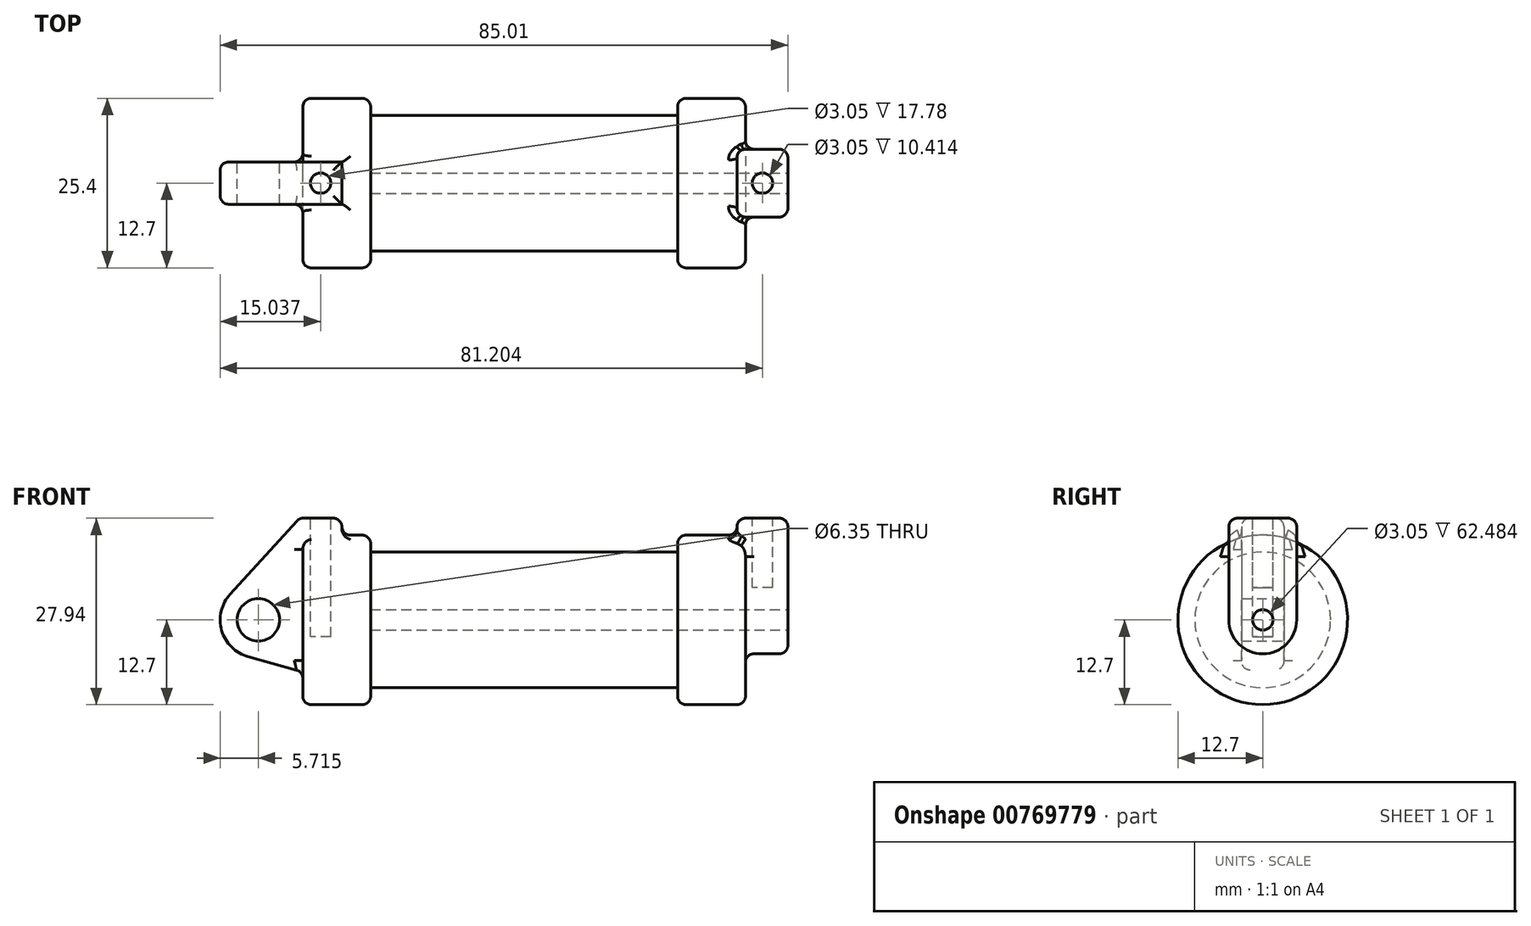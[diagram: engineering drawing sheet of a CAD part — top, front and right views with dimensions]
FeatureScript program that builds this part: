
annotation { "Feature Type Name" : "Feature", "Feature Type Description" : "" }
export const myFeature = defineFeature(function(context is Context, id is Id, definition is map)
    precondition{}
    {
        {
            var Q0;
            Q0=qCreatedBy(makeId("Front.planeOp"),FACE);
            var sketch = newSketch(context, id + "F0", { "sketchPlane" : qUnion([Q0])});
            skLineSegment(sketch, "E0", {"start": v(0, 0) * mm, "end": v(0, 12.7) * mm});
            skLineSegment(sketch, "E1", {"start": v(0, 12.7) * mm, "end": v(10.16, 12.7) * mm});
            skLineSegment(sketch, "E2", {"start": v(10.16, 12.7) * mm, "end": v(10.16, 10.16) * mm});
            skLineSegment(sketch, "E3", {"start": v(10.16, 10.16) * mm, "end": v(56.13, 10.16) * mm});
            skLineSegment(sketch, "E4", {"start": v(56.13, 10.16) * mm, "end": v(56.13, 12.7) * mm});
            skLineSegment(sketch, "E5", {"start": v(56.13, 12.7) * mm, "end": v(66.3, 12.7) * mm});
            skLineSegment(sketch, "E6", {"start": v(66.3, 12.7) * mm, "end": v(66.3, 0) * mm});
            skLineSegment(sketch, "E7", {"start": v(66.3, 0) * mm, "end": v(0, 0) * mm});
            skLineSegment(sketch, "E8", {"start": v(5.84, 15.24) * mm, "end": v(-0.5, 15.24) * mm});
            skLineSegment(sketch, "E9", {"start": v(-0.5, 15.24) * mm, "end": v(-10.88, 3.85) * mm});
            skLineSegment(sketch, "E10", {"start": v(0, 0) * mm, "end": v(-6.65, 0) * mm});
            skCircle(sketch, "E11", {"center": v(-6.65, 0) * mm, "radius": 5.72 * mm});
            skCircle(sketch, "E12", {"center": v(-6.65, 0) * mm, "radius": 3.18 * mm});
            skLineSegment(sketch, "E13", {"start": v(5.84, 15.24) * mm, "end": v(5.84, -9.4) * mm});
            skLineSegment(sketch, "E14", {"start": v(5.84, -9.4) * mm, "end": v(-8.18, -5.5) * mm});
            skSolve(sketch);
        }
        {
            var Q0;
            {var subQ0=sQuery(id+"F0.wireOp",EDGE,"E2");Q0=makeQuery(id+"F0.imprint","IMPRINT",FACE,{"disambiguationData":[TD([[makeQuery(id+"F0.imprint","IMPRINT",EDGE,{"derivedFrom":subQ0}),-1.0]])]});}
            var Q1;
            {var subQ0=sQuery(id+"F0.wireOp",EDGE,"E0");Q1=makeQuery(id+"F0.imprint","IMPRINT",FACE,{"disambiguationData":[TD([[makeQuery(id+"F0.imprint","IMPRINT",EDGE,{"derivedFrom":subQ0}),-1.0]])]});}
            var Q2;
            Q2=sQuery(id+"F0.wireOp",EDGE,"E7");
            revolve(context, id + "F1", {"surfaceOperationType" : NewSurfaceOperationType.NEW, "entities" : qUnion([Q0, Q1]), "axis" : qUnion([Q2]), "revolveType" : RevolveType.FULL});
        }
        {
            var Q0;
            {var subQ1=sQuery(id+"F0.wireOp",EDGE,"E0");Q0=makeQuery(id+"F0.imprint","IMPRINT",FACE,{"disambiguationData":[TD([[makeQuery(id+"F0.imprint","IMPRINT",EDGE,{"derivedFrom":subQ1}),1.0]])]});}
            var Q1;
            {var subQ0=sQuery(id+"F0.wireOp",EDGE,"E0");Q1=makeQuery(id+"F0.imprint","IMPRINT",FACE,{"disambiguationData":[TD([[makeQuery(id+"F0.imprint","IMPRINT",EDGE,{"derivedFrom":subQ0}),-1.0]])]});}
            var Q2;
            {var subQ0=sQuery(id+"F0.wireOp",EDGE,"E14");Q2=makeQuery(id+"F0.imprint","IMPRINT",FACE,{"disambiguationData":[TD([[makeQuery(id+"F0.imprint","IMPRINT",EDGE,{"derivedFrom":subQ0}),-1.0]])]});}
            var Q3;
            {var subQ5=sQuery(id+"F0.wireOp",EDGE,"E12");Q3=makeQuery(id+"F0.imprint","IMPRINT",FACE,{"disambiguationData":[TD([[makeQuery(id+"F0.imprint","IMPRINT",EDGE,{"derivedFrom":subQ5}),-1.0]])]});}
            extrude(context, id + "F2", {"entities" : qUnion([Q0, Q1, Q2, Q3]), "endBound" : BoundingType.SYMMETRIC, "depth" : 6.35 * mm, "offsetDistance" : 25.4 * mm});
        }
        {
            var Q0;
            Q0=makeQuery(id+"F1.opRevolve","SWEPT_BODY",BODY,{"disambiguationData":[OSD([sQuery(id+"F0.wireOp",EDGE,"E0"),sQuery(id+"F0.wireOp",EDGE,"E1"),sQuery(id+"F0.wireOp",EDGE,"E2"),sQuery(id+"F0.wireOp",EDGE,"E3"),sQuery(id+"F0.wireOp",EDGE,"E4"),sQuery(id+"F0.wireOp",EDGE,"E5"),sQuery(id+"F0.wireOp",EDGE,"E6"),sQuery(id+"F0.wireOp",EDGE,"E7")])]});
            var Q1;
            Q1=makeQuery(id+"F2.opExtrude","SWEPT_BODY",BODY,{"disambiguationData":[OSD([sQuery(id+"F0.wireOp",EDGE,"E8"),sQuery(id+"F0.wireOp",EDGE,"E9"),sQuery(id+"F0.wireOp",EDGE,"E11"),sQuery(id+"F0.wireOp",EDGE,"E12"),sQuery(id+"F0.wireOp",EDGE,"E13"),sQuery(id+"F0.wireOp",EDGE,"E14")])]});
            booleanBodies(context, id + "F3", {"operationType" : BooleanOperationType.UNION, "tools" : qUnion([Q0, Q1])});
        }
        {
            var Q0;
            Q0=makeQuery(id+"F1.opRevolve","SWEPT_FACE",FACE,{"disambiguationData":[OSD([sQuery(id+"F0.wireOp",EDGE,"E6")])]});
            var sketch = newSketch(context, id + "F4", { "sketchPlane" : qUnion([Q0])});
            skCircle(sketch, "E15", {"center": v(0, 0) * mm, "radius": 1.52 * mm});
            skCircle(sketch, "E16", {"center": v(0, 0) * mm, "radius": 5.08 * mm});
            skLineSegment(sketch, "E17", {"start": v(-5.08, 0) * mm, "end": v(-5.08, 15.24) * mm});
            skLineSegment(sketch, "E18", {"start": v(5.08, 0) * mm, "end": v(5.08, 15.24) * mm});
            skLineSegment(sketch, "E19", {"start": v(5.08, 15.24) * mm, "end": v(-5.08, 15.24) * mm});
            skSolve(sketch);
        }
        {
            var Q0;
            {var subQ0=sQuery(id+"F4.wireOp",EDGE,"E19");Q0=makeQuery(id+"F4.imprint","IMPRINT",FACE,{"disambiguationData":[TD([[makeQuery(id+"F4.imprint","IMPRINT",EDGE,{"derivedFrom":subQ0}),1.0]])]});}
            var Q1;
            {var subQ0=sQuery(id+"F4.wireOp",EDGE,"E17");var subQ1=sQuery(id+"F4.wireOp",EDGE,"E16");var subQ2=makeQuery(id+"F4.imprint","INTERSECT",VERTEX,{"derivedFrom":[subQ1,subQ0]});Q1=makeQuery(id+"F4.imprint","IMPRINT",FACE,{"disambiguationData":[TD([[makeQuery(id+"F4.imprint","IMPRINT",EDGE,{"disambiguationData":[TD([[subQ2,1.0]])],"derivedFrom":subQ1}),-1.0]])]});}
            var Q2;
            Q2=makeQuery(id+"F4.imprint","IMPRINT",FACE,{"disambiguationData":[TD([[makeQuery(id+"F4.imprint","IMPRINT",EDGE,{"derivedFrom":sQuery(id+"F4.wireOp",EDGE,"E15")}),-1.0]])]});
            extrude(context, id + "F5", {"entities" : qUnion([Q0, Q1, Q2]), "operationType" : NewBodyOperationType.ADD, "oppositeDirection" : true, "depth" : 1.27 * mm, "offsetDistance" : 25.4 * mm, "hasSecondDirection" : true, "secondDirectionOppositeDirection" : false, "secondDirectionDepth" : 6.35 * mm});
        }
        {
            var Q0;
            Q0=makeQuery(id+"F5.boolean.opBoolean","SPLIT",FACE,{"disambiguationData":[TD([makeQuery(id+"F5.opExtrude","SWEPT_FACE",FACE,{"disambiguationData":[OSD([sQuery(id+"F4.wireOp",EDGE,"E15")])]})])],"derivedFrom":makeQuery(id+"F1.opRevolve","SWEPT_FACE",FACE,{"disambiguationData":[OSD([sQuery(id+"F0.wireOp",EDGE,"E6")])]})});
            var Q1;
            Q1=makeQuery(id+"F1.opRevolve","SWEPT_FACE",FACE,{"disambiguationData":[OSD([sQuery(id+"F0.wireOp",EDGE,"E2")])]});
            extrude(context, id + "F6", {"entities" : qUnion([Q0]), "operationType" : NewBodyOperationType.REMOVE, "endBound" : BoundingType.UP_TO_SURFACE, "oppositeDirection" : true, "depth" : 25.4 * mm, "endBoundEntityFace" : qUnion([Q1]), "offsetDistance" : 25.4 * mm});
        }
        {
            var Q0;
            Q0=makeQuery(id+"F2.opExtrude","SWEPT_FACE",FACE,{"disambiguationData":[OSD([sQuery(id+"F0.wireOp",EDGE,"E8")])]});
            var sketch = newSketch(context, id + "F7", { "sketchPlane" : qUnion([Q0])});
            skCircle(sketch, "E20", {"center": v(2.67, 0) * mm, "radius": 1.52 * mm});
            skPoint(sketch, "E20.centerSnap0", {"position": v(5.84, 0) * mm});
            skPoint(sketch, "E20.centerSnap1", {"position": v(2.67, -3.18) * mm});
            skSolve(sketch);
        }
        {
            var Q0;
            Q0=makeQuery(id+"F7.imprint","IMPRINT",FACE,{"disambiguationData":[TD([[makeQuery(id+"F7.imprint","IMPRINT",EDGE,{"derivedFrom":sQuery(id+"F7.wireOp",EDGE,"E20")}),1.0]])]});
            extrude(context, id + "F8", {"entities" : qUnion([Q0]), "operationType" : NewBodyOperationType.REMOVE, "oppositeDirection" : true, "depth" : 17.78 * mm, "offsetDistance" : 25.4 * mm});
        }
        {
            var Q0;
            Q0=makeQuery(id+"F5.opExtrude","SWEPT_FACE",FACE,{"disambiguationData":[OSD([sQuery(id+"F4.wireOp",EDGE,"E19")])]});
            var sketch = newSketch(context, id + "F9", { "sketchPlane" : qUnion([Q0])});
            skCircle(sketch, "E21", {"center": v(68.83, 0) * mm, "radius": 1.52 * mm});
            skPoint(sketch, "E21.centerSnap0", {"position": v(68.83, -5.08) * mm});
            skPoint(sketch, "E21.centerSnap1", {"position": v(72.64, 0) * mm});
            skSolve(sketch);
        }
        {
            var Q0;
            Q0=makeQuery(id+"F9.imprint","IMPRINT",FACE,{"disambiguationData":[TD([[makeQuery(id+"F9.imprint","IMPRINT",EDGE,{"derivedFrom":sQuery(id+"F9.wireOp",EDGE,"E21")}),1.0]])]});
            extrude(context, id + "F10", {"entities" : qUnion([Q0]), "operationType" : NewBodyOperationType.REMOVE, "oppositeDirection" : true, "depth" : 10.4 * mm, "offsetDistance" : 25.4 * mm});
        }
        {
            var Q0;
            Q0=makeQuery(id+"F1.opRevolve","SWEPT_EDGE",EDGE,{"disambiguationData":[OSD([sQuery(id+"F0.wireOp",EDGE,"E1"),sQuery(id+"F0.wireOp",EDGE,"E2")])]});
            var Q1;
            Q1=makeQuery(id+"F1.opRevolve","SWEPT_EDGE",EDGE,{"disambiguationData":[OSD([sQuery(id+"F0.wireOp",EDGE,"E0"),sQuery(id+"F0.wireOp",EDGE,"E1")])]});
            var Q2;
            Q2=makeQuery(id+"F1.opRevolve","SWEPT_EDGE",EDGE,{"disambiguationData":[OSD([sQuery(id+"F0.wireOp",EDGE,"E4"),sQuery(id+"F0.wireOp",EDGE,"E5")])]});
            var Q3;
            Q3=makeQuery(id+"F1.opRevolve","SWEPT_EDGE",EDGE,{"disambiguationData":[OSD([sQuery(id+"F0.wireOp",EDGE,"E5"),sQuery(id+"F0.wireOp",EDGE,"E6")])]});
            fillet(context, id + "F11", {"entities" : qUnion([Q0, Q1, Q2, Q3]), "radius" : 1.27 * mm, "tangentPropagation" : true, "allowEdgeOverflow" : false});
        }
        {
            var Q0;
            Q0=makeQuery(id+"F2.opExtrude","SWEPT_FACE",FACE,{"disambiguationData":[OSD([sQuery(id+"F0.wireOp",EDGE,"E9")])]});
            var Q1;
            Q1=makeQuery(id+"F2.opExtrude","SWEPT_FACE",FACE,{"disambiguationData":[OSD([sQuery(id+"F0.wireOp",EDGE,"E11")])]});
            var Q2;
            Q2=makeQuery(id+"F2.opExtrude","SWEPT_FACE",FACE,{"disambiguationData":[OSD([sQuery(id+"F0.wireOp",EDGE,"E14")])]});
            var Q3;
            Q3=makeQuery(id+"F3.opBoolean","INTERSECT",EDGE,{"derivedFrom":[makeQuery(id+"F1.opRevolve","SWEPT_FACE",FACE,{"disambiguationData":[OSD([sQuery(id+"F0.wireOp",EDGE,"E0")])]}),makeQuery(id+"F2.opExtrude","CAP_FACE",FACE,{"disambiguationData":[OSD([sQuery(id+"F0.wireOp",EDGE,"E8"),sQuery(id+"F0.wireOp",EDGE,"E9"),sQuery(id+"F0.wireOp",EDGE,"E11"),sQuery(id+"F0.wireOp",EDGE,"E12"),sQuery(id+"F0.wireOp",EDGE,"E13"),sQuery(id+"F0.wireOp",EDGE,"E14")])],"isStart":false})]});
            var Q4;
            Q4=makeQuery(id+"F11.opFillet","BLEND_EDGE",EDGE,{"blendedFrom":[makeQuery(id+"F1.opRevolve","SWEPT_EDGE",EDGE,{"disambiguationData":[OSD([sQuery(id+"F0.wireOp",EDGE,"E0"),sQuery(id+"F0.wireOp",EDGE,"E1")])]}),makeQuery(id+"F2.opExtrude","CAP_FACE",FACE,{"disambiguationData":[OSD([sQuery(id+"F0.wireOp",EDGE,"E8"),sQuery(id+"F0.wireOp",EDGE,"E9"),sQuery(id+"F0.wireOp",EDGE,"E11"),sQuery(id+"F0.wireOp",EDGE,"E12"),sQuery(id+"F0.wireOp",EDGE,"E13"),sQuery(id+"F0.wireOp",EDGE,"E14")])],"isStart":false})],"blendedInto":[makeQuery(id+"F2.opExtrude","CAP_FACE",FACE,{"disambiguationData":[OSD([sQuery(id+"F0.wireOp",EDGE,"E8"),sQuery(id+"F0.wireOp",EDGE,"E9"),sQuery(id+"F0.wireOp",EDGE,"E11"),sQuery(id+"F0.wireOp",EDGE,"E12"),sQuery(id+"F0.wireOp",EDGE,"E13"),sQuery(id+"F0.wireOp",EDGE,"E14")])],"isStart":false})]});
            var Q5;
            Q5=makeQuery(id+"F3.opBoolean","INTERSECT",EDGE,{"derivedFrom":[makeQuery(id+"F1.opRevolve","SWEPT_FACE",FACE,{"disambiguationData":[OSD([sQuery(id+"F0.wireOp",EDGE,"E1")])]}),makeQuery(id+"F2.opExtrude","CAP_FACE",FACE,{"disambiguationData":[OSD([sQuery(id+"F0.wireOp",EDGE,"E8"),sQuery(id+"F0.wireOp",EDGE,"E9"),sQuery(id+"F0.wireOp",EDGE,"E11"),sQuery(id+"F0.wireOp",EDGE,"E12"),sQuery(id+"F0.wireOp",EDGE,"E13"),sQuery(id+"F0.wireOp",EDGE,"E14")])],"isStart":false})]});
            var Q6;
            Q6=makeQuery(id+"F3.opBoolean","INTERSECT",EDGE,{"derivedFrom":[makeQuery(id+"F1.opRevolve","SWEPT_FACE",FACE,{"disambiguationData":[OSD([sQuery(id+"F0.wireOp",EDGE,"E1")])]}),makeQuery(id+"F2.opExtrude","SWEPT_FACE",FACE,{"disambiguationData":[OSD([sQuery(id+"F0.wireOp",EDGE,"E13")])]})]});
            var Q7;
            Q7=makeQuery(id+"F2.opExtrude","CAP_EDGE",EDGE,{"disambiguationData":[OSD([sQuery(id+"F0.wireOp",EDGE,"E8")])],"isStart":false});
            var Q8;
            Q8=makeQuery(id+"F2.opExtrude","SWEPT_EDGE",EDGE,{"disambiguationData":[OSD([sQuery(id+"F0.wireOp",EDGE,"E8"),sQuery(id+"F0.wireOp",EDGE,"E13")])]});
            var Q9;
            Q9=makeQuery(id+"F2.opExtrude","CAP_EDGE",EDGE,{"disambiguationData":[OSD([sQuery(id+"F0.wireOp",EDGE,"E8")])],"isStart":true});
            var Q10;
            Q10=makeQuery(id+"F3.opBoolean","INTERSECT",EDGE,{"derivedFrom":[makeQuery(id+"F1.opRevolve","SWEPT_FACE",FACE,{"disambiguationData":[OSD([sQuery(id+"F0.wireOp",EDGE,"E1")])]}),makeQuery(id+"F2.opExtrude","CAP_FACE",FACE,{"disambiguationData":[OSD([sQuery(id+"F0.wireOp",EDGE,"E8"),sQuery(id+"F0.wireOp",EDGE,"E9"),sQuery(id+"F0.wireOp",EDGE,"E11"),sQuery(id+"F0.wireOp",EDGE,"E12"),sQuery(id+"F0.wireOp",EDGE,"E13"),sQuery(id+"F0.wireOp",EDGE,"E14")])],"isStart":true})]});
            var Q11;
            Q11=makeQuery(id+"F11.opFillet","BLEND_EDGE",EDGE,{"blendedFrom":[makeQuery(id+"F1.opRevolve","SWEPT_EDGE",EDGE,{"disambiguationData":[OSD([sQuery(id+"F0.wireOp",EDGE,"E0"),sQuery(id+"F0.wireOp",EDGE,"E1")])]}),makeQuery(id+"F2.opExtrude","CAP_FACE",FACE,{"disambiguationData":[OSD([sQuery(id+"F0.wireOp",EDGE,"E8"),sQuery(id+"F0.wireOp",EDGE,"E9"),sQuery(id+"F0.wireOp",EDGE,"E11"),sQuery(id+"F0.wireOp",EDGE,"E12"),sQuery(id+"F0.wireOp",EDGE,"E13"),sQuery(id+"F0.wireOp",EDGE,"E14")])],"isStart":true})],"blendedInto":[makeQuery(id+"F2.opExtrude","CAP_FACE",FACE,{"disambiguationData":[OSD([sQuery(id+"F0.wireOp",EDGE,"E8"),sQuery(id+"F0.wireOp",EDGE,"E9"),sQuery(id+"F0.wireOp",EDGE,"E11"),sQuery(id+"F0.wireOp",EDGE,"E12"),sQuery(id+"F0.wireOp",EDGE,"E13"),sQuery(id+"F0.wireOp",EDGE,"E14")])],"isStart":true})]});
            var Q12;
            Q12=makeQuery(id+"F3.opBoolean","INTERSECT",EDGE,{"derivedFrom":[makeQuery(id+"F1.opRevolve","SWEPT_FACE",FACE,{"disambiguationData":[OSD([sQuery(id+"F0.wireOp",EDGE,"E0")])]}),makeQuery(id+"F2.opExtrude","CAP_FACE",FACE,{"disambiguationData":[OSD([sQuery(id+"F0.wireOp",EDGE,"E8"),sQuery(id+"F0.wireOp",EDGE,"E9"),sQuery(id+"F0.wireOp",EDGE,"E11"),sQuery(id+"F0.wireOp",EDGE,"E12"),sQuery(id+"F0.wireOp",EDGE,"E13"),sQuery(id+"F0.wireOp",EDGE,"E14")])],"isStart":true})]});
            fillet(context, id + "F12", {"entities" : qUnion([Q0, Q1, Q2, Q3, Q4, Q5, Q6, Q7, Q8, Q9, Q10, Q11, Q12]), "radius" : 1.27 * mm, "allowEdgeOverflow" : false});
        }
        {
            var Q0;
            Q0=makeQuery(id+"F5.opExtrude","CAP_EDGE",EDGE,{"disambiguationData":[OSD([sQuery(id+"F4.wireOp",EDGE,"E17")])],"isStart":false});
            var Q1;
            Q1=makeQuery(id+"F5.boolean.opBoolean","INTERSECT",EDGE,{"derivedFrom":[makeQuery(id+"F1.opRevolve","SWEPT_FACE",FACE,{"disambiguationData":[OSD([sQuery(id+"F0.wireOp",EDGE,"E5")])]}),makeQuery(id+"F5.opExtrude","CAP_FACE",FACE,{"disambiguationData":[OSD([sQuery(id+"F4.wireOp",EDGE,"E15"),sQuery(id+"F4.wireOp",EDGE,"E16"),sQuery(id+"F4.wireOp",EDGE,"E17"),sQuery(id+"F4.wireOp",EDGE,"E18"),sQuery(id+"F4.wireOp",EDGE,"E19")])],"isStart":false})]});
            var Q2;
            Q2=makeQuery(id+"F5.opExtrude","CAP_EDGE",EDGE,{"disambiguationData":[OSD([sQuery(id+"F4.wireOp",EDGE,"E19")])],"isStart":false});
            var Q3;
            Q3=makeQuery(id+"F5.opExtrude","CAP_EDGE",EDGE,{"disambiguationData":[OSD([sQuery(id+"F4.wireOp",EDGE,"E18")])],"isStart":false});
            var Q4;
            Q4=makeQuery(id+"F5.opExtrude","SWEPT_EDGE",EDGE,{"disambiguationData":[OSD([sQuery(id+"F4.wireOp",EDGE,"E18"),sQuery(id+"F4.wireOp",EDGE,"E19")])]});
            var Q5;
            Q5=makeQuery(id+"F5.opExtrude","SWEPT_EDGE",EDGE,{"disambiguationData":[OSD([sQuery(id+"F4.wireOp",EDGE,"E17"),sQuery(id+"F4.wireOp",EDGE,"E19")])]});
            var Q6;
            Q6=makeQuery(id+"F5.opExtrude","CAP_EDGE",EDGE,{"disambiguationData":[OSD([sQuery(id+"F4.wireOp",EDGE,"E17")])],"isStart":true});
            var Q7;
            Q7=makeQuery(id+"F11.opFillet","BLEND_EDGE",EDGE,{"blendedFrom":[makeQuery(id+"F1.opRevolve","SWEPT_EDGE",EDGE,{"disambiguationData":[OSD([sQuery(id+"F0.wireOp",EDGE,"E5"),sQuery(id+"F0.wireOp",EDGE,"E6")])]}),makeQuery(id+"F5.opExtrude","SWEPT_FACE",FACE,{"disambiguationData":[OSD([sQuery(id+"F4.wireOp",EDGE,"E17")])]})],"blendedInto":[makeQuery(id+"F5.opExtrude","SWEPT_FACE",FACE,{"disambiguationData":[OSD([sQuery(id+"F4.wireOp",EDGE,"E17")])]})]});
            var Q8;
            Q8=makeQuery(id+"F5.boolean.opBoolean","INTERSECT",EDGE,{"derivedFrom":[makeQuery(id+"F1.opRevolve","SWEPT_FACE",FACE,{"disambiguationData":[OSD([sQuery(id+"F0.wireOp",EDGE,"E6")])]}),makeQuery(id+"F5.opExtrude","SWEPT_FACE",FACE,{"disambiguationData":[OSD([sQuery(id+"F4.wireOp",EDGE,"E17")])]})]});
            var Q9;
            Q9=makeQuery(id+"F5.boolean.opBoolean","INTERSECT",EDGE,{"derivedFrom":[makeQuery(id+"F1.opRevolve","SWEPT_FACE",FACE,{"disambiguationData":[OSD([sQuery(id+"F0.wireOp",EDGE,"E6")])]}),makeQuery(id+"F5.opExtrude","SWEPT_FACE",FACE,{"disambiguationData":[OSD([sQuery(id+"F4.wireOp",EDGE,"E16")])]})]});
            var Q10;
            Q10=makeQuery(id+"F5.opExtrude","CAP_EDGE",EDGE,{"disambiguationData":[OSD([sQuery(id+"F4.wireOp",EDGE,"E16")])],"isStart":true});
            var Q11;
            Q11=makeQuery(id+"F5.opExtrude","CAP_EDGE",EDGE,{"disambiguationData":[OSD([sQuery(id+"F4.wireOp",EDGE,"E18")])],"isStart":true});
            var Q12;
            Q12=makeQuery(id+"F5.boolean.opBoolean","INTERSECT",EDGE,{"derivedFrom":[makeQuery(id+"F1.opRevolve","SWEPT_FACE",FACE,{"disambiguationData":[OSD([sQuery(id+"F0.wireOp",EDGE,"E6")])]}),makeQuery(id+"F5.opExtrude","SWEPT_FACE",FACE,{"disambiguationData":[OSD([sQuery(id+"F4.wireOp",EDGE,"E18")])]})]});
            var Q13;
            Q13=makeQuery(id+"F11.opFillet","BLEND_EDGE",EDGE,{"blendedFrom":[makeQuery(id+"F1.opRevolve","SWEPT_EDGE",EDGE,{"disambiguationData":[OSD([sQuery(id+"F0.wireOp",EDGE,"E5"),sQuery(id+"F0.wireOp",EDGE,"E6")])]}),makeQuery(id+"F5.opExtrude","SWEPT_FACE",FACE,{"disambiguationData":[OSD([sQuery(id+"F4.wireOp",EDGE,"E18")])]})],"blendedInto":[makeQuery(id+"F5.opExtrude","SWEPT_FACE",FACE,{"disambiguationData":[OSD([sQuery(id+"F4.wireOp",EDGE,"E18")])]})]});
            var Q14;
            Q14=makeQuery(id+"F5.opExtrude","CAP_EDGE",EDGE,{"disambiguationData":[OSD([sQuery(id+"F4.wireOp",EDGE,"E19")])],"isStart":true});
            fillet(context, id + "F13", {"entities" : qUnion([Q0, Q1, Q2, Q3, Q4, Q5, Q6, Q7, Q8, Q9, Q10, Q11, Q12, Q13, Q14]), "radius" : 1.27 * mm, "allowEdgeOverflow" : false});
        }
    });
